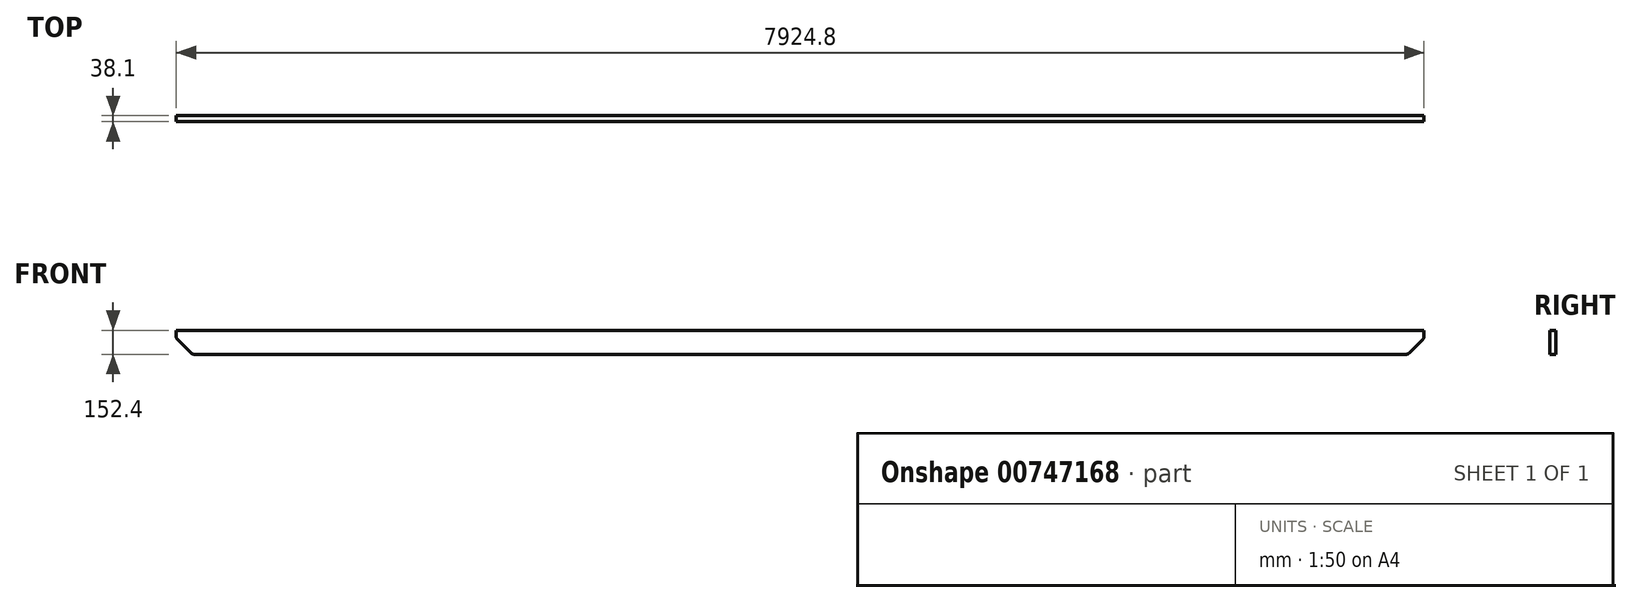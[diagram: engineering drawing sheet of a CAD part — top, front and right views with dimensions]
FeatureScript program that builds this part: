
annotation { "Feature Type Name" : "Feature", "Feature Type Description" : "" }
export const myFeature = defineFeature(function(context is Context, id is Id, definition is map)
    precondition{}
    {
        {
            var Q0;
            Q0=qCreatedBy(makeId("Right.planeOp"),FACE);
            var sketch = newSketch(context, id + "F0", { "sketchPlane" : qUnion([Q0])});
            skLineSegment(sketch, "E0.bottom", {"start": v(-43.25, 108.82) * mm, "end": v(-5.15, 108.82) * mm});
            skLineSegment(sketch, "E0.top", {"start": v(-43.25, -43.58) * mm, "end": v(-5.15, -43.58) * mm});
            skLineSegment(sketch, "E0.left", {"start": v(-43.25, 108.82) * mm, "end": v(-43.25, -43.58) * mm});
            skLineSegment(sketch, "E0.right", {"start": v(-5.15, 108.82) * mm, "end": v(-5.15, -43.58) * mm});
            skSolve(sketch);
        }
        {
            var Q0;
            Q0 = qSketchRegion(id + "F0", true);
            extrude(context, id + "F1", {"entities" : qUnion([Q0]), "oppositeDirection" : true, "depth" : 7924.8 * mm, "offsetDistance" : 25.4 * mm});
        }
        {
            var Q0;
            Q0=makeQuery(id+"F1.opExtrude","CAP_EDGE",EDGE,{"disambiguationData":[OSD([sQuery(id+"F0.wireOp",EDGE,"E0.top")])],"isStart":true});
            var Q1;
            Q1=makeQuery(id+"F1.opExtrude","CAP_EDGE",EDGE,{"disambiguationData":[OSD([sQuery(id+"F0.wireOp",EDGE,"E0.top")])],"isStart":false});
            chamfer(context, id + "F2", {"entities" : qUnion([Q0, Q1]), "width" : 101.6 * mm, "tangentPropagation" : true});
        }
        {
            var Q0;
            {var subQ0=sQuery(id+"F0.wireOp",EDGE,"E0.top");Q0=makeQuery(id+"F2.opChamfer","BLEND_EDGE",EDGE,{"blendedFrom":[makeQuery(id+"F1.opExtrude","CAP_EDGE",EDGE,{"disambiguationData":[OSD([subQ0])],"isStart":true}),makeQuery(id+"F1.opExtrude","CAP_FACE",FACE,{"disambiguationData":[OSD([sQuery(id+"F0.wireOp",EDGE,"E0.bottom"),subQ0,sQuery(id+"F0.wireOp",EDGE,"E0.left"),sQuery(id+"F0.wireOp",EDGE,"E0.right")])],"isStart":true})],"blendedInto":[makeQuery(id+"F1.opExtrude","CAP_FACE",FACE,{"disambiguationData":[OSD([sQuery(id+"F0.wireOp",EDGE,"E0.bottom"),subQ0,sQuery(id+"F0.wireOp",EDGE,"E0.left"),sQuery(id+"F0.wireOp",EDGE,"E0.right")])],"isStart":true})]});}
            var Q1;
            {var subQ0=sQuery(id+"F0.wireOp",EDGE,"E0.top");Q1=makeQuery(id+"F2.opChamfer","BLEND_EDGE",EDGE,{"blendedFrom":[makeQuery(id+"F1.opExtrude","CAP_EDGE",EDGE,{"disambiguationData":[OSD([subQ0])],"isStart":true}),makeQuery(id+"F1.opExtrude","SWEPT_FACE",FACE,{"disambiguationData":[OSD([subQ0])]})],"blendedInto":[makeQuery(id+"F1.opExtrude","SWEPT_FACE",FACE,{"disambiguationData":[OSD([subQ0])]})]});}
            var Q2;
            {var subQ0=sQuery(id+"F0.wireOp",EDGE,"E0.top");Q2=makeQuery(id+"F2.opChamfer","BLEND_EDGE",EDGE,{"blendedFrom":[makeQuery(id+"F1.opExtrude","CAP_EDGE",EDGE,{"disambiguationData":[OSD([subQ0])],"isStart":false}),makeQuery(id+"F1.opExtrude","CAP_FACE",FACE,{"disambiguationData":[OSD([sQuery(id+"F0.wireOp",EDGE,"E0.bottom"),subQ0,sQuery(id+"F0.wireOp",EDGE,"E0.left"),sQuery(id+"F0.wireOp",EDGE,"E0.right")])],"isStart":false})],"blendedInto":[makeQuery(id+"F1.opExtrude","CAP_FACE",FACE,{"disambiguationData":[OSD([sQuery(id+"F0.wireOp",EDGE,"E0.bottom"),subQ0,sQuery(id+"F0.wireOp",EDGE,"E0.left"),sQuery(id+"F0.wireOp",EDGE,"E0.right")])],"isStart":false})]});}
            var Q3;
            {var subQ0=sQuery(id+"F0.wireOp",EDGE,"E0.top");Q3=makeQuery(id+"F2.opChamfer","BLEND_EDGE",EDGE,{"blendedFrom":[makeQuery(id+"F1.opExtrude","CAP_EDGE",EDGE,{"disambiguationData":[OSD([subQ0])],"isStart":false}),makeQuery(id+"F1.opExtrude","SWEPT_FACE",FACE,{"disambiguationData":[OSD([subQ0])]})],"blendedInto":[makeQuery(id+"F1.opExtrude","SWEPT_FACE",FACE,{"disambiguationData":[OSD([subQ0])]})]});}
            fillet(context, id + "F3", {"entities" : qUnion([Q0, Q1, Q2, Q3]), "radius" : 25.4 * mm, "tangentPropagation" : true, "allowEdgeOverflow" : false});
        }
    });
